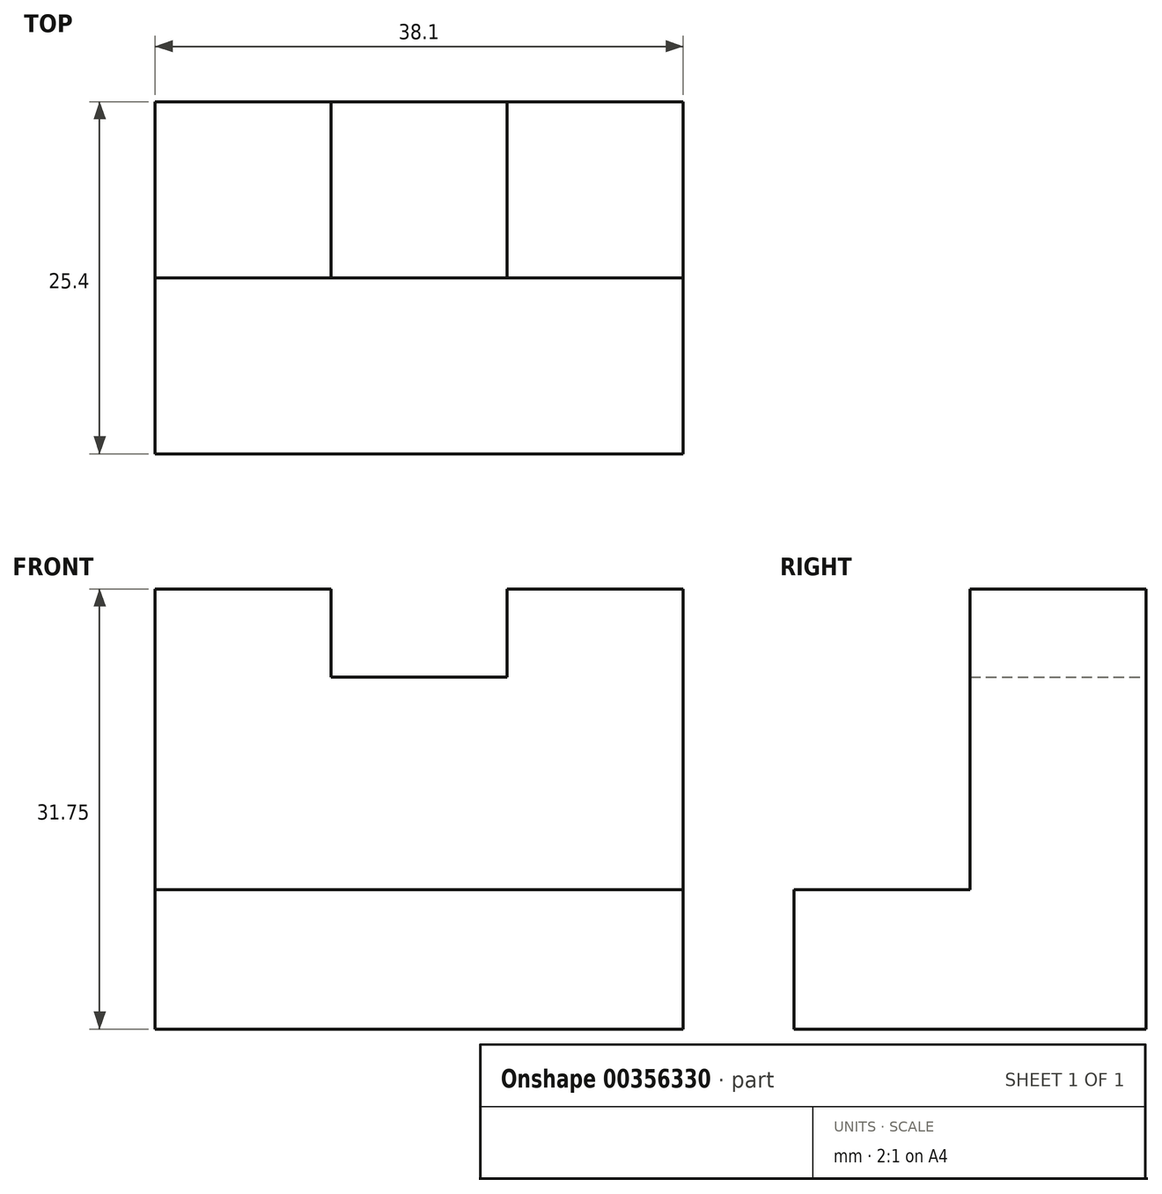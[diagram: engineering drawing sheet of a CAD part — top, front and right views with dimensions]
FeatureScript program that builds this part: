
annotation { "Feature Type Name" : "Feature", "Feature Type Description" : "" }
export const myFeature = defineFeature(function(context is Context, id is Id, definition is map)
    precondition{}
    {
        {
            var Q0;
            Q0=qCreatedBy(makeId("Front.planeOp"),FACE);
            var sketch = newSketch(context, id + "F0", { "sketchPlane" : qUnion([Q0])});
            skLineSegment(sketch, "E0", {"start": v(0, 0) * mm, "end": v(38.1, 0) * mm});
            skLineSegment(sketch, "E1", {"start": v(38.1, 0) * mm, "end": v(38.1, 31.75) * mm});
            skLineSegment(sketch, "E2", {"start": v(38.1, 31.75) * mm, "end": v(25.4, 31.75) * mm});
            skLineSegment(sketch, "E3", {"start": v(25.4, 31.75) * mm, "end": v(25.4, 25.4) * mm});
            skLineSegment(sketch, "E4", {"start": v(25.4, 25.4) * mm, "end": v(12.7, 25.4) * mm});
            skLineSegment(sketch, "E5", {"start": v(12.7, 25.4) * mm, "end": v(12.7, 31.75) * mm});
            skLineSegment(sketch, "E6", {"start": v(12.7, 31.75) * mm, "end": v(0, 31.75) * mm});
            skLineSegment(sketch, "E7", {"start": v(0, 0) * mm, "end": v(0, 31.75) * mm});
            skSolve(sketch);
        }
        {
            var Q0;
            Q0=makeQuery(id+"F0.imprint","IMPRINT",FACE,{"disambiguationData":[TD([[makeQuery(id+"F0.imprint","IMPRINT",EDGE,{"derivedFrom":sQuery(id+"F0.wireOp",EDGE,"E0")}),1.0]])]});
            extrude(context, id + "F1", {"entities" : qUnion([Q0]), "depth" : 25.4 * mm});
        }
        {
            var Q0;
            Q0=makeQuery(id+"F1.opExtrude","CAP_FACE",FACE,{"disambiguationData":[OSD([sQuery(id+"F0.wireOp",EDGE,"E0"),sQuery(id+"F0.wireOp",EDGE,"E1"),sQuery(id+"F0.wireOp",EDGE,"E2"),sQuery(id+"F0.wireOp",EDGE,"E3"),sQuery(id+"F0.wireOp",EDGE,"E4"),sQuery(id+"F0.wireOp",EDGE,"E5"),sQuery(id+"F0.wireOp",EDGE,"E6"),sQuery(id+"F0.wireOp",EDGE,"E7")])],"isStart":false});
            var sketch = newSketch(context, id + "F2", { "sketchPlane" : qUnion([Q0])});
            skLineSegment(sketch, "E8", {"start": v(0, 10.06) * mm, "end": v(38.1, 10.06) * mm});
            skSolve(sketch);
        }
        {
            var Q0;
            {var subQ1=sQuery(id+"F2.wireOp",EDGE,"E8");Q0=makeQuery(id+"F2.imprint","IMPRINT",FACE,{"disambiguationData":[TD([[makeQuery(id+"F2.imprint","IMPRINT",EDGE,{"derivedFrom":subQ1}),1.0]])]});}
            extrude(context, id + "F3", {"entities" : qUnion([Q0]), "operationType" : NewBodyOperationType.REMOVE, "oppositeDirection" : true, "depth" : 12.7 * mm});
        }
    });
